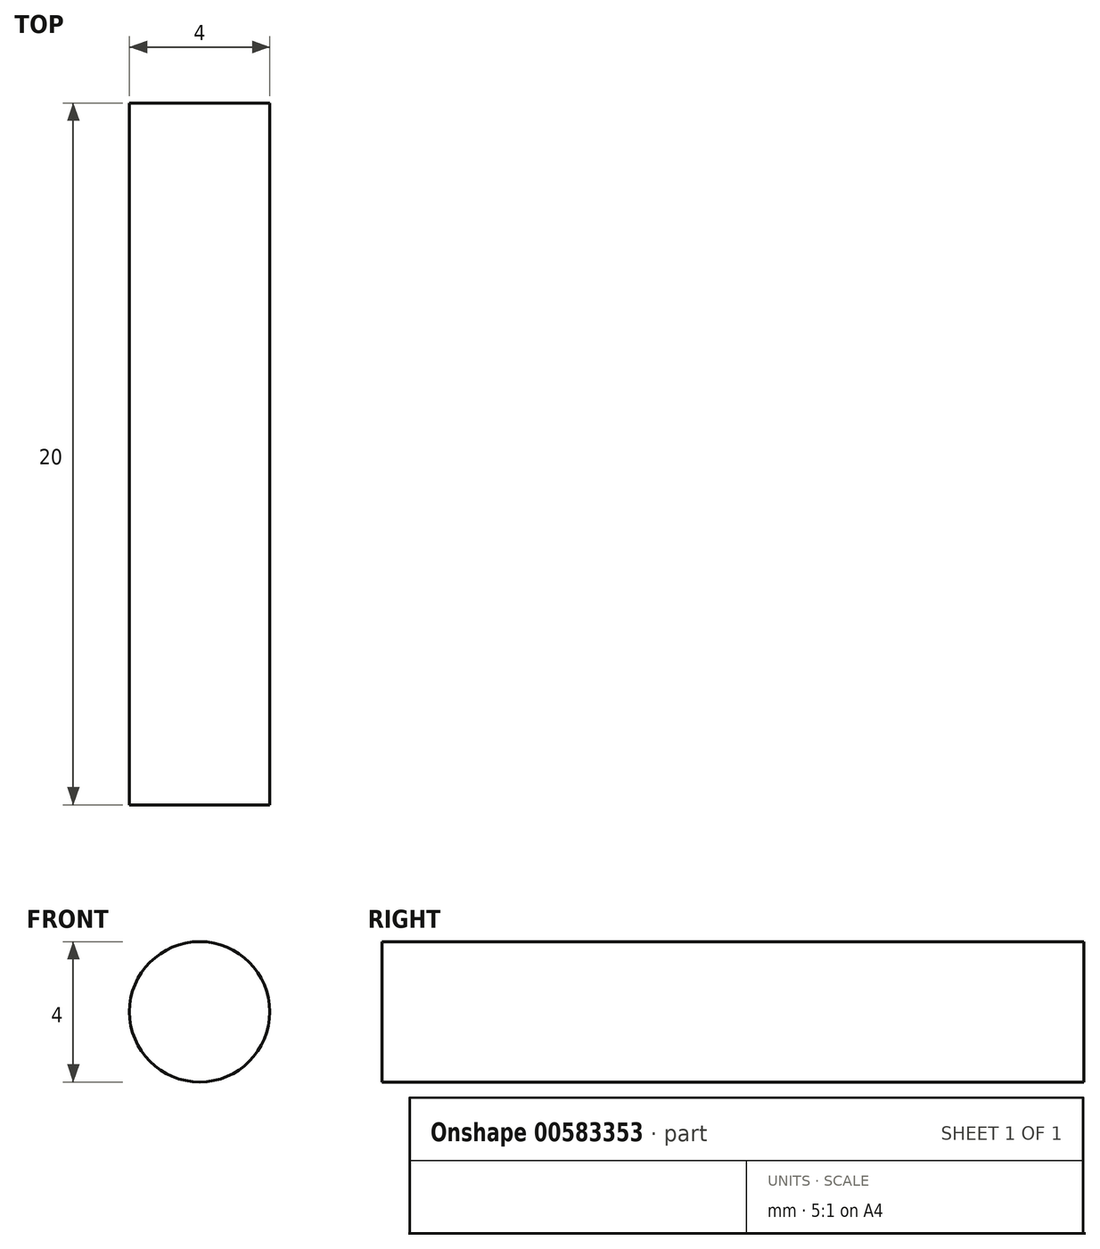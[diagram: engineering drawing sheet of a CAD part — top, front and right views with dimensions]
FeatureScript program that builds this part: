
annotation { "Feature Type Name" : "Feature", "Feature Type Description" : "" }
export const myFeature = defineFeature(function(context is Context, id is Id, definition is map)
    precondition{}
    {
        {
            var Q0;
            Q0=qCreatedBy(makeId("Front.planeOp"),FACE);
            var sketch = newSketch(context, id + "F0", { "sketchPlane" : qUnion([Q0])});
            skCircle(sketch, "E0", {"center": v(0, 0) * mm, "radius": 2 * mm});
            skSolve(sketch);
        }
        {
            var Q0;
            Q0=makeQuery(id+"F0.imprint","IMPRINT",FACE,{"disambiguationData":[TD([[makeQuery(id+"F0.imprint","IMPRINT",EDGE,{"derivedFrom":sQuery(id+"F0.wireOp",EDGE,"E0")}),1.0]])]});
            extrude(context, id + "F1", {"entities" : qUnion([Q0]), "depth" : 20 * mm, "offsetDistance" : 25 * mm});
        }
    });
